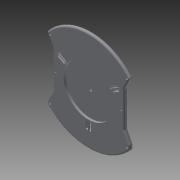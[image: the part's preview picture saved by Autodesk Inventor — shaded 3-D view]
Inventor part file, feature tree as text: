
AUTODESK INVENTOR PART (.ipt)
format: ipt  version: 2015 (Build 190159000, 159)  size: 740,864 bytes
history: native  units: mm
features: extrude x21, sketch x21, fillet x2
ambient origin geometry x8: Origin, YZ Plane, XZ Plane, XY Plane, X Axis, Y Axis, Z Axis, Center Point
bodies: Solid1 (feature_tree)
feature tree (44):
  extrude  "Extrusion1"  Depth=4.0mm
  extrude  "Extrusion2"  Depth=4.0mm
  extrude  "Extrusion3"  Depth=4.0mm
  extrude  "Extrusion4"  Depth=4.0mm
  extrude  "Extrusion5"  Depth=4.0mm
  extrude  "Extrusion6"  Depth=4.0mm
  extrude  "Extrusion7"  Depth=4.0mm
  sketch  "Sketch8"  dims[d14=4.0mm d15=4.0mm]
  sketch  "Sketch9"  dims[d16=4.0mm d17=4.0mm]
  sketch  "Sketch10"  dims[d18=4.0mm d19=4.0mm]
  extrude  "Extrusion8"  Depth=4.0mm
  extrude  "Extrusion9"  Depth=4.0mm
  extrude  "Extrusion10"  Depth=4.0mm
  extrude  "Extrusion11"  Depth=4.0mm
  extrude  "Extrusion12"  Depth=4.0mm
  extrude  "Extrusion13"  Depth=2.0mm TaperAngle=0.0deg
  extrude  "Extrusion14"  Depth=8.0mm TaperAngle=0.0deg
  extrude  "Extrusion15"  Depth=10.0mm TaperAngle=0.0deg
  extrude  "Extrusion16"  Depth=8.0mm
  sketch  "Sketch18"  dims[d41=11.3mm d42=0.0mm d43=11.3mm d44=0.0mm]
  extrude  "Extrusion17"  Depth=11.3mm TaperAngle=0.0deg
  extrude  "Extrusion18"  Depth=11.3mm TaperAngle=0.0deg
  extrude  "Extrusion19"  Depth=100.0mm
  extrude  "Extrusion20"  Depth=6.0mm
  extrude  "Extrusion21"  Depth=1.0mm
  fillet  "Fillet1"  Radius=3.0mm
  fillet  "Fillet2"  Radius=11.3mm
  sketch  "Sketch1"  dims[d0=4.0mm d1=4.0mm]
  sketch  "Sketch2"  dims[d2=4.0mm d3=4.0mm]
  sketch  "Sketch3"  dims[d4=4.0mm d5=4.0mm]
  sketch  "Sketch4"  dims[d6=4.0mm d7=4.0mm]
  sketch  "Sketch5"  dims[d8=4.0mm d9=4.0mm]
  sketch  "Sketch6"  dims[d10=4.0mm d11=4.0mm]
  sketch  "Sketch7"  dims[d12=4.0mm d13=4.0mm]
  sketch  "Sketch11"  dims[d20=4.0mm d21=4.0mm]
  sketch  "Sketch12"  dims[d22=4.0mm d23=4.0mm]
  sketch  "Sketch13"  dims[d24=4.0mm d25=2.0mm d26=0.0mm]
  sketch  "Sketch14"  dims[d27=1.3mm d28=0.0mm d29=8.0mm d30=0.0mm]
  sketch  "Sketch15"  dims[d31=10.0mm d32=0.0mm d33=10.0mm d34=0.0mm]
  sketch  "Sketch16"  dims[d35=3.0mm d36=8.0mm]
  sketch  "Sketch17"  dims[d37=11.3mm d38=0.0mm d39=11.3mm d40=0.0mm]
  sketch  "Sketch19"  dims[d45=100.0mm d46=100.0mm]
  sketch  "Sketch20"  dims[d47=11.3mm d48=0.0mm d49=6.0mm]
  sketch  "Sketch21"  dims[d50=11.3mm d51=0.0mm d52=3.0mm d53=3.0mm d54=11.3mm d55=0.0mm d56=11.3mm d57=0.0mm d58=1.3mm d59=0.0mm d60=120.0mm d63=60.191mm d65=37.2mm d66=14.209mm d67=91.5mm d68=8.0mm d69=0.0mm d70=3.8mm d71=0.0mm d72=10.0mm d73=20.0mm d74=10.0mm d75=14.0mm d87=20.0mm d88=10.0mm d89=20.0mm d90=10.0mm d91=14.0mm d92=10.0mm d93=14.0mm d94=10.0mm d95=10.0mm d96=0.0mm d97=30.0deg d98=2.5mm d99=2.5mm d100=2.5mm d101=2.5mm d102=2.5mm d103=2.5mm d104=2.5mm d105=0.0mm d106=20.0mm d107=0.0mm d108=20.0mm d109=0.0mm d110=20.0mm d111=0.0mm d112=3.0mm d113=14.0mm d114=1.0mm]
